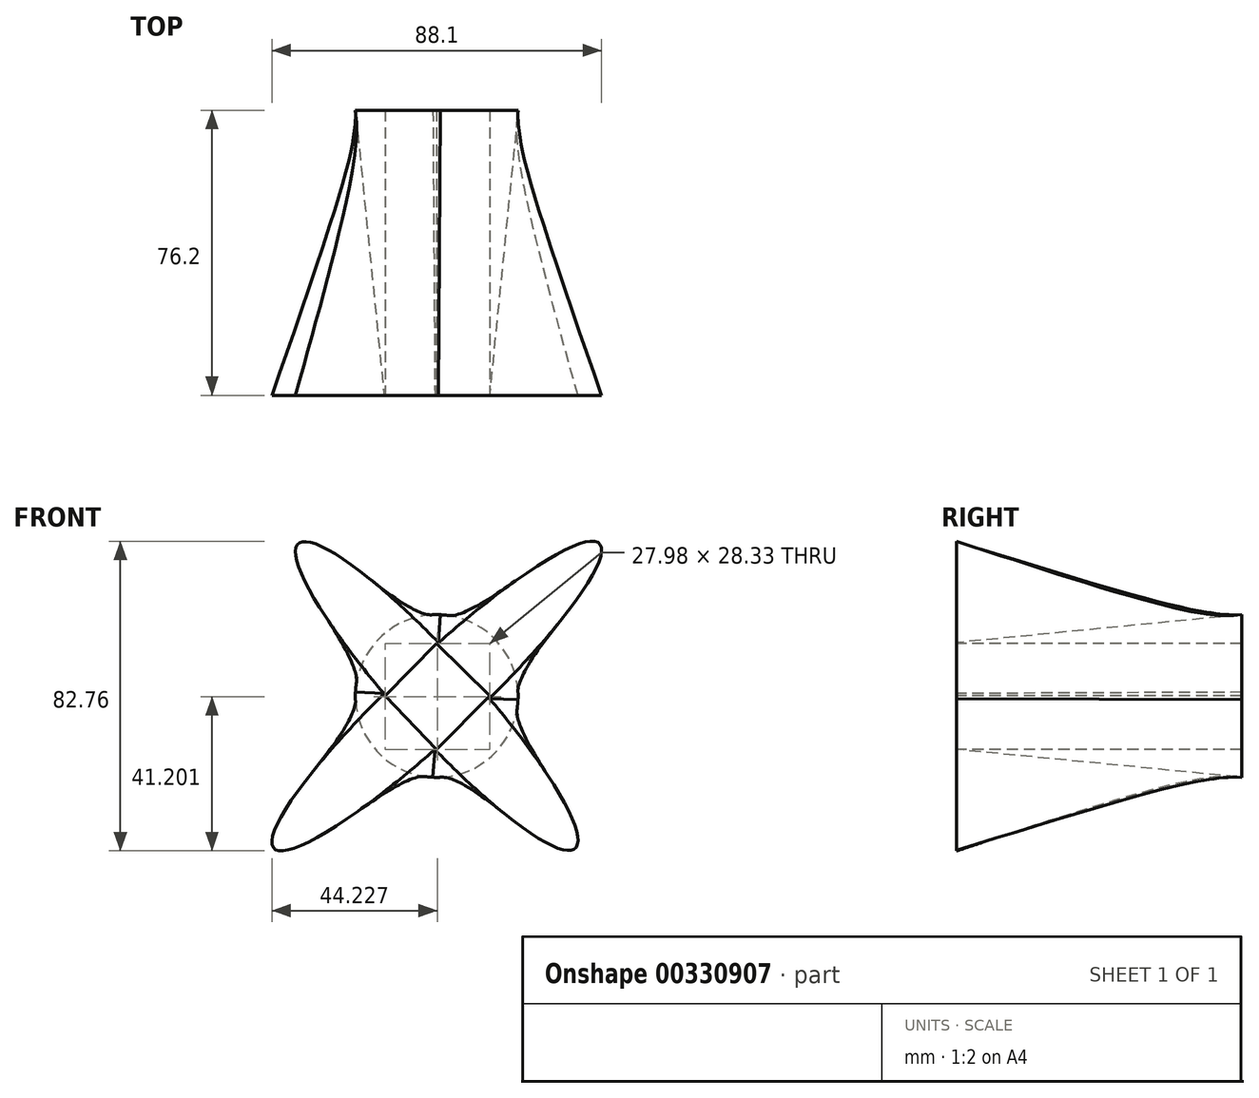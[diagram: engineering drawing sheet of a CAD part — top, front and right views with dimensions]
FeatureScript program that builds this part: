
annotation { "Feature Type Name" : "Feature", "Feature Type Description" : "" }
export const myFeature = defineFeature(function(context is Context, id is Id, definition is map)
    precondition{}
    {
        {
            var Q0;
            Q0=qCreatedBy(makeId("Front.planeOp"),FACE);
            cPlane(context, id + "F0", {"entities" : qUnion([Q0]), "cplaneType" : CPlaneType.OFFSET, "offset" : 76.2 * mm, "width" : 152.4 * mm, "height" : 152.4 * mm});
        }
        {
            var Q0;
            Q0=qCreatedBy(makeId("Front.planeOp"),FACE);
            var sketch = newSketch(context, id + "F1", { "sketchPlane" : qUnion([Q0])});
            skCircle(sketch, "E0", {"center": v(0, 0) * mm, "radius": 21.74 * mm});
            skSolve(sketch);
        }
        {
            var Q0;
            Q0=qCreatedBy(id+"F0.planeOp",FACE);
            var sketch = newSketch(context, id + "F2", { "sketchPlane" : qUnion([Q0])});
            skEllipse(sketch, "E1", {"center": v(0, 0) * mm, "majorRadius": 59.57 * mm, "minorRadius": 10.24 * mm, "majorAxis": v(-0.73, -0.68)});
            skEllipse(sketch, "E2", {"center": v(0, 0) * mm, "majorRadius": 55 * mm, "minorRadius": 10.15 * mm, "majorAxis": v(0.67, -0.74)});
            skSolve(sketch);
        }
        {
            var Q0;
            Q0 = qSketchRegion(id + "F1", true);
            var Q1;
            Q1 = qSketchRegion(id + "F2", true);
            loft(context, id + "F3", {"sheetProfilesArray" : [{ "sheetProfileEntities" : qUnion([Q0]) }, { "sheetProfileEntities" : qUnion([Q1]) }]});
        }
        {
            var Q0;
            Q0=qCreatedBy(id+"F0.planeOp",FACE);
            var sketch = newSketch(context, id + "F4", { "sketchPlane" : qUnion([Q0])});
            skLineSegment(sketch, "E3", {"start": v(-13.81, 0) * mm, "end": v(0, 13.99) * mm});
            skLineSegment(sketch, "E4", {"start": v(0, 13.99) * mm, "end": v(14.17, 0) * mm});
            skLineSegment(sketch, "E5", {"start": v(14.17, 0) * mm, "end": v(0, -14.35) * mm});
            skLineSegment(sketch, "E6", {"start": v(0, -14.35) * mm, "end": v(-13.81, 0) * mm});
            skSolve(sketch);
        }
        {
            var Q0;
            Q0 = qSketchRegion(id + "F4", true);
            extrude(context, id + "F5", {"entities" : qUnion([Q0]), "operationType" : NewBodyOperationType.REMOVE, "endBound" : BoundingType.THROUGH_ALL, "oppositeDirection" : true, "depth" : 92.46 * mm});
        }
    });
